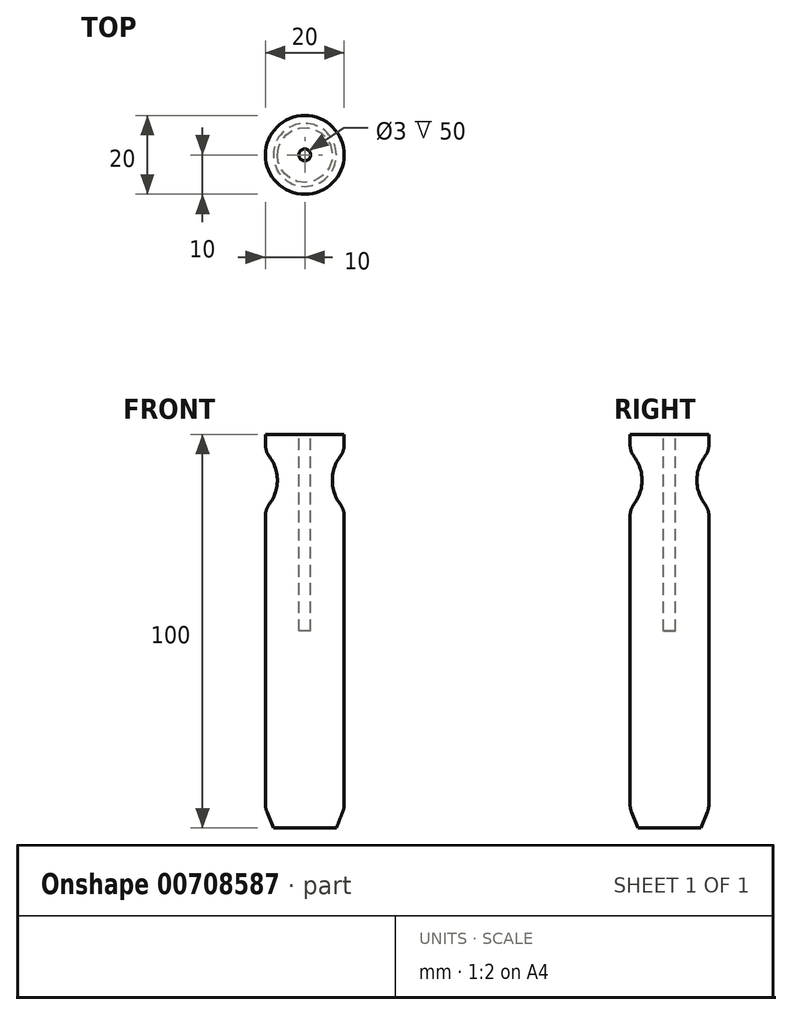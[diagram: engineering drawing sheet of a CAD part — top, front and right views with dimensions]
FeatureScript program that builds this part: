
annotation { "Feature Type Name" : "Feature", "Feature Type Description" : "" }
export const myFeature = defineFeature(function(context is Context, id is Id, definition is map)
    precondition{}
    {
        {
            assignVariable(context, id + "F0", {"name" : "Length", "anyValue" : 100});
        }
        {
            assignVariable(context, id + "F1", {"name" : "HoleDepth", "anyValue" : 50});
        }
        {
            var Q0;
            Q0=qCreatedBy(makeId("Top.planeOp"),FACE);
            var sketch = newSketch(context, id + "F2", { "sketchPlane" : qUnion([Q0])});
            skCircle(sketch, "E0", {"center": v(0, 0) * mm, "radius": 10 * mm});
            skSolve(sketch);
        }
        {
            var Q0;
            Q0=makeQuery(id+"F2.imprint","IMPRINT",FACE,{"disambiguationData":[TD([[makeQuery(id+"F2.imprint","IMPRINT",EDGE,{"derivedFrom":sQuery(id+"F2.wireOp",EDGE,"E0")}),1.0]])]});
            extrude(context, id + "F3", {"entities" : qUnion([Q0]), "depth" : (getVariable(context, 'Length')) * mm, "offsetDistance" : 25 * mm});
        }
        {
            var Q0;
            Q0=makeQuery(id+"F3.opExtrude","CAP_EDGE",EDGE,{"disambiguationData":[OSD([sQuery(id+"F2.wireOp",EDGE,"E0")])],"isStart":true});
            chamfer(context, id + "F4", {"entities" : qUnion([Q0]), "chamferType" : ChamferType.TWO_OFFSETS, "width1" : 5 * mm, "oppositeDirection" : false, "width2" : 2 * mm, "tangentPropagation" : true});
        }
        {
            var Q0;
            Q0=makeQuery(id+"F3.opExtrude","CAP_FACE",FACE,{"disambiguationData":[OSD([sQuery(id+"F2.wireOp",EDGE,"E0")])],"isStart":false});
            var sketch = newSketch(context, id + "F5", { "sketchPlane" : qUnion([Q0])});
            skCircle(sketch, "E1", {"center": v(0, 0) * mm, "radius": 1.5 * mm});
            skSolve(sketch);
        }
        {
            var Q0;
            Q0 = qSketchRegion(id + "F5", true);
            extrude(context, id + "F6", {"entities" : qUnion([Q0]), "operationType" : NewBodyOperationType.REMOVE, "oppositeDirection" : true, "depth" : (getVariable(context, 'HoleDepth')) * mm, "offsetDistance" : 25 * mm});
        }
        {
            var Q0;
            Q0=qCreatedBy(makeId("Front.planeOp"),FACE);
            var sketch = newSketch(context, id + "F7", { "sketchPlane" : qUnion([Q0])});
            skLineSegment(sketch, "E2", {"start": v(0, 100) * mm, "end": v(0, 0) * mm, "construction": true});
            skLineSegment(sketch, "E3.0", {"start": v(-10, 100) * mm, "end": v(10, 100) * mm, "construction": true});
            skLineSegment(sketch, "E4.0", {"start": v(-10, 5) * mm, "end": v(10, 5) * mm, "construction": true});
            skLineSegment(sketch, "E5", {"start": v(10, 100) * mm, "end": v(10, 5) * mm, "construction": true});
            skArc(sketch, "E6", {"start": v(13.18, 97.59) * mm, "mid": v(6.98, 88.34) * mm, "end": v(13.18, 79.09) * mm});
            skLineSegment(sketch, "E7", {"start": v(13.18, 97.59) * mm, "end": v(13.18, 79.09) * mm});
            skPoint(sketch, "E8", {"position": v(10, 95.5) * mm});
            skSolve(sketch);
        }
        {
            var Q0;
            Q0 = qSketchRegion(id + "F7", true);
            var Q1;
            Q1=sQuery(id+"F7.wireOp",EDGE,"E2");
            revolve(context, id + "F8", {"operationType" : NewBodyOperationType.REMOVE, "surfaceOperationType" : NewSurfaceOperationType.NEW, "entities" : qUnion([Q0]), "axis" : qUnion([Q1]), "revolveType" : RevolveType.FULL, "oppositeDirection" : true});
        }
        {
            var Q0;
            Q0=makeQuery(id+"F8.boolean.opBoolean","INTERSECT",EDGE,{"disambiguationData":[OD(1.0)],"derivedFrom":[makeQuery(id+"F3.opExtrude","SWEPT_FACE",FACE,{"disambiguationData":[OSD([sQuery(id+"F2.wireOp",EDGE,"E0")])]}),makeQuery(id+"F8.opRevolve","SWEPT_FACE",FACE,{"disambiguationData":[OSD([sQuery(id+"F7.wireOp",EDGE,"E6")])]})]});
            fillet(context, id + "F9", {"entities" : qUnion([Q0]), "radius" : 5 * mm, "tangentPropagation" : true, "allowEdgeOverflow" : false});
        }
        {
            var Q0;
            Q0=makeQuery(id+"F8.boolean.opBoolean","INTERSECT",EDGE,{"disambiguationData":[OD(0.0)],"derivedFrom":[makeQuery(id+"F3.opExtrude","SWEPT_FACE",FACE,{"disambiguationData":[OSD([sQuery(id+"F2.wireOp",EDGE,"E0")])]}),makeQuery(id+"F8.opRevolve","SWEPT_FACE",FACE,{"disambiguationData":[OSD([sQuery(id+"F7.wireOp",EDGE,"E6")])]})]});
            fillet(context, id + "F10", {"entities" : qUnion([Q0]), "radius" : 5 * mm, "tangentPropagation" : true, "allowEdgeOverflow" : false});
        }
        {
            var Q0;
            {var subQ0=sQuery(id+"F2.wireOp",EDGE,"E0");Q0=makeQuery(id+"F4.opChamfer","BLEND_EDGE",EDGE,{"blendedFrom":[makeQuery(id+"F3.opExtrude","CAP_EDGE",EDGE,{"disambiguationData":[OSD([subQ0])],"isStart":true}),makeQuery(id+"F3.opExtrude","SWEPT_FACE",FACE,{"disambiguationData":[OSD([subQ0])]})],"blendedInto":[makeQuery(id+"F3.opExtrude","SWEPT_FACE",FACE,{"disambiguationData":[OSD([subQ0])]})]});}
            fillet(context, id + "F11", {"entities" : qUnion([Q0]), "radius" : 5 * mm, "tangentPropagation" : true, "allowEdgeOverflow" : false});
        }
    });
